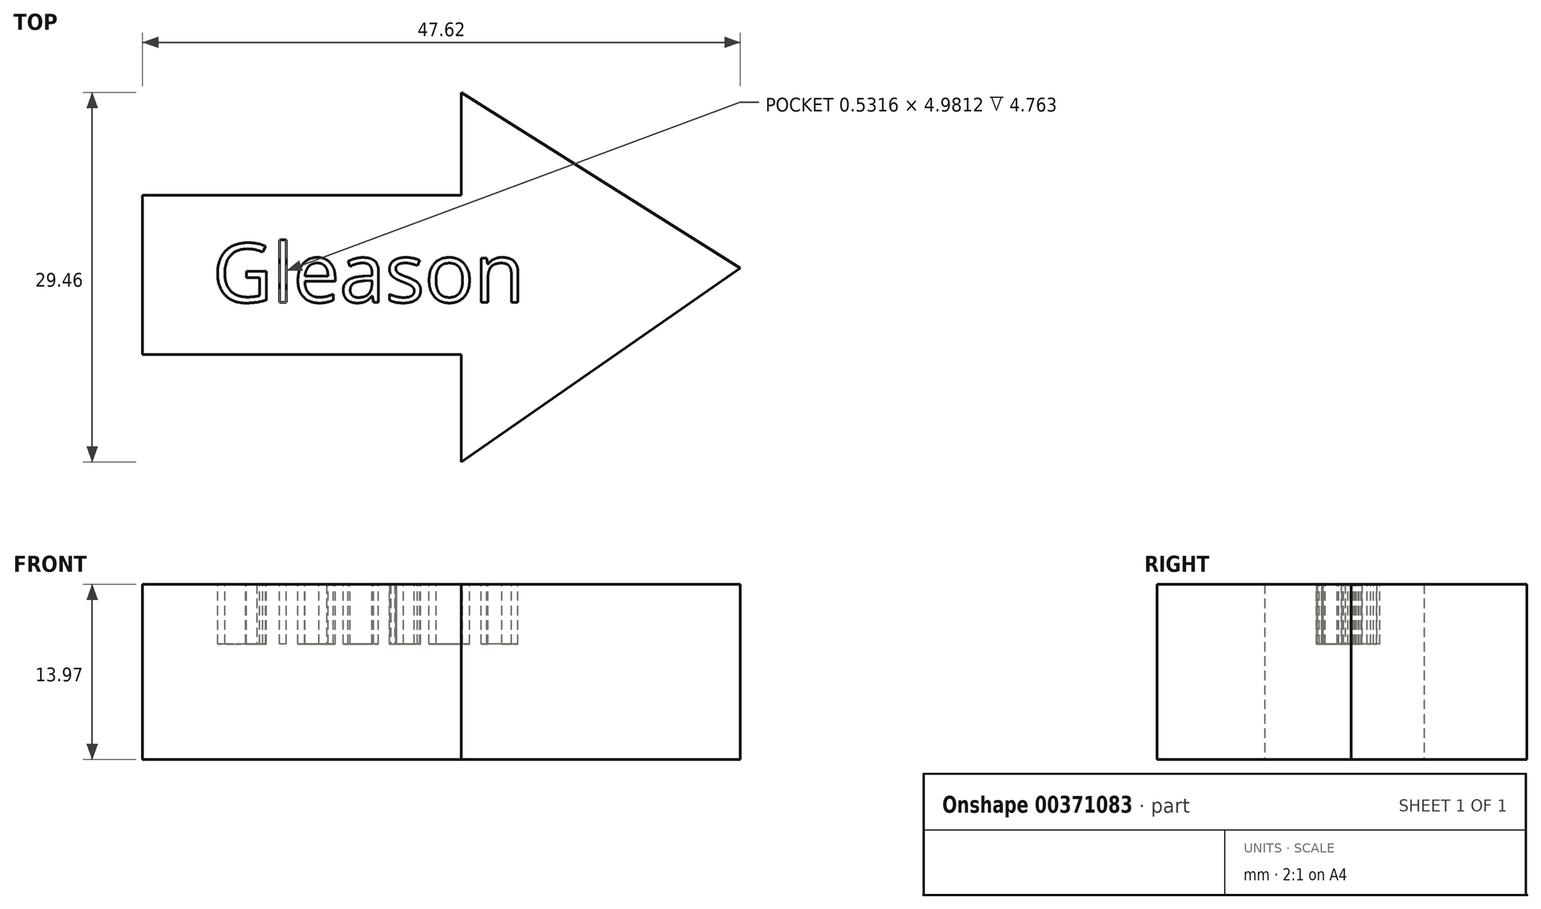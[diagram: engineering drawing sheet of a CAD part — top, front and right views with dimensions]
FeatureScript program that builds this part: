
annotation { "Feature Type Name" : "Feature", "Feature Type Description" : "" }
export const myFeature = defineFeature(function(context is Context, id is Id, definition is map)
    precondition{}
    {
        {
            var Q0;
            Q0=qCreatedBy(makeId("Top.planeOp"),FACE);
            var sketch = newSketch(context, id + "F0", { "sketchPlane" : qUnion([Q0])});
            skLineSegment(sketch, "E0", {"start": v(-63.3, 30.84) * mm, "end": v(-37.9, 30.84) * mm});
            skLineSegment(sketch, "E1", {"start": v(-37.9, 30.84) * mm, "end": v(-37.9, 18.14) * mm});
            skLineSegment(sketch, "E2", {"start": v(-63.3, 30.84) * mm, "end": v(-63.3, 18.14) * mm});
            skLineSegment(sketch, "E3", {"start": v(-63.3, 18.14) * mm, "end": v(-37.9, 18.14) * mm});
            skLineSegment(sketch, "E4", {"start": v(-37.9, 30.84) * mm, "end": v(-37.9, 39.05) * mm});
            skLineSegment(sketch, "E5", {"start": v(-37.9, 39.05) * mm, "end": v(-15.68, 25.05) * mm});
            skLineSegment(sketch, "E6", {"start": v(-15.68, 25.05) * mm, "end": v(-37.9, 9.6) * mm});
            skLineSegment(sketch, "E7", {"start": v(-37.9, 18.14) * mm, "end": v(-37.9, 9.6) * mm});
            skSolve(sketch);
        }
        {
            var Q0;
            Q0 = qSketchRegion(id + "F0", true);
            extrude(context, id + "F1", {"entities" : qUnion([Q0]), "depth" : 13.97 * mm});
        }
        {
            var Q0;
            Q0=makeQuery(id+"F1.opExtrude","CAP_FACE",FACE,{"disambiguationData":[OSD([sQuery(id+"F0.wireOp",EDGE,"E0"),sQuery(id+"F0.wireOp",EDGE,"E2"),sQuery(id+"F0.wireOp",EDGE,"E3"),sQuery(id+"F0.wireOp",EDGE,"E4"),sQuery(id+"F0.wireOp",EDGE,"E5"),sQuery(id+"F0.wireOp",EDGE,"E6"),sQuery(id+"F0.wireOp",EDGE,"E7")])],"isStart":false});
            var sketch = newSketch(context, id + "F2", { "sketchPlane" : qUnion([Q0])});
            skText(sketch, "E8", { "text": "Gleason", "fontName": "OpenSans-Regular.ttf"});
            const initialGuessF2  = {"E8": [-0.05772, 0.02233, 1, 0, 0.00472]};
            skSetInitialGuess(sketch, initialGuessF2);
            skSolve(sketch);
        }
        {
            var Q0;
            Q0 = qSketchRegion(id + "F2", true);
            extrude(context, id + "F3", {"entities" : qUnion([Q0]), "operationType" : NewBodyOperationType.REMOVE, "oppositeDirection" : true, "depth" : 4.76 * mm});
        }
    });
